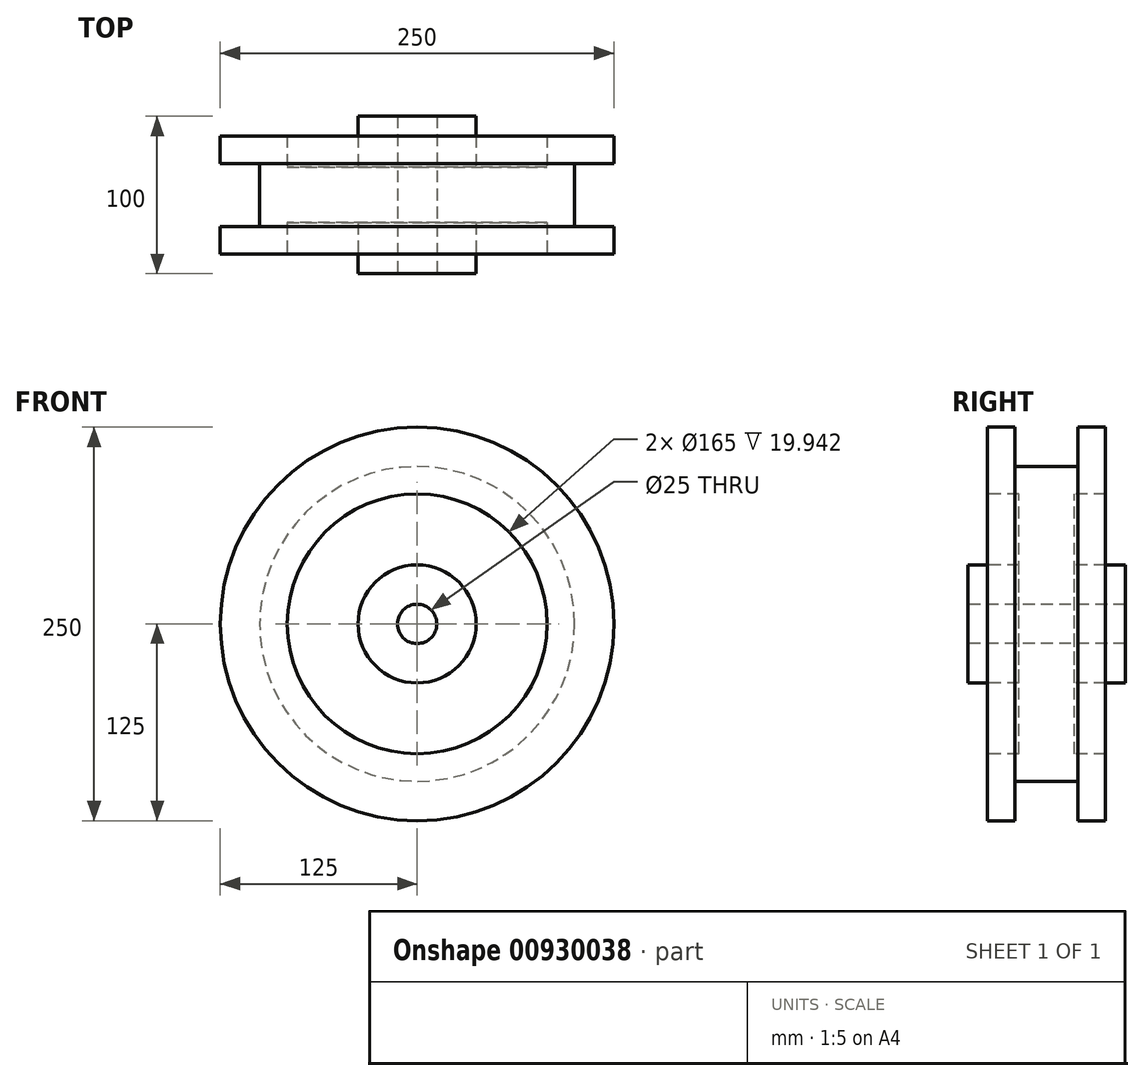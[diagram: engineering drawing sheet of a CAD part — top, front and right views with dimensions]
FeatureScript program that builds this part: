
annotation { "Feature Type Name" : "Feature", "Feature Type Description" : "" }
export const myFeature = defineFeature(function(context is Context, id is Id, definition is map)
    precondition{}
    {
        {
            var Q0;
            Q0=qCreatedBy(makeId("Right.planeOp"),FACE);
            var sketch = newSketch(context, id + "F0", { "sketchPlane" : qUnion([Q0])});
            skLineSegment(sketch, "E0", {"start": v(-83.35, 0) * mm, "end": v(75.08, 0) * mm, "construction": true});
            skLineSegment(sketch, "E1", {"start": v(0, 0) * mm, "end": v(0, 73.26) * mm, "construction": true});
            skLineSegment(sketch, "E2", {"start": v(-37.5, 125) * mm, "end": v(-20, 125) * mm});
            skLineSegment(sketch, "E3", {"start": v(-20, 125) * mm, "end": v(-20, 100) * mm});
            skLineSegment(sketch, "E4", {"start": v(-37.5, 125) * mm, "end": v(-37.5, 82.5) * mm});
            skLineSegment(sketch, "E5", {"start": v(-37.5, 82.5) * mm, "end": v(-17.56, 82.5) * mm});
            skLineSegment(sketch, "E6", {"start": v(-17.56, 82.5) * mm, "end": v(-17.56, 37.5) * mm});
            skLineSegment(sketch, "E7", {"start": v(-17.56, 37.5) * mm, "end": v(-50, 37.5) * mm});
            skLineSegment(sketch, "E8", {"start": v(-50, 37.5) * mm, "end": v(-50, 12.5) * mm});
            skLineSegment(sketch, "E9", {"start": v(-50, 12.5) * mm, "end": v(0, 12.5) * mm});
            skLineSegment(sketch, "E10.MirrorCS", {"start": v(37.5, 82.5) * mm, "end": v(17.56, 82.5) * mm});
            skLineSegment(sketch, "E11.MirrorCS", {"start": v(37.5, 125) * mm, "end": v(37.5, 82.5) * mm});
            skLineSegment(sketch, "E12.MirrorCS", {"start": v(50, 12.5) * mm, "end": v(0, 12.5) * mm});
            skLineSegment(sketch, "E13.MirrorCS", {"start": v(50, 37.5) * mm, "end": v(50, 12.5) * mm});
            skLineSegment(sketch, "E14.MirrorCS", {"start": v(20, 125) * mm, "end": v(20, 100) * mm});
            skLineSegment(sketch, "E15.MirrorCS", {"start": v(17.56, 37.5) * mm, "end": v(50, 37.5) * mm});
            skLineSegment(sketch, "E16.MirrorCS", {"start": v(37.5, 125) * mm, "end": v(20, 125) * mm});
            skLineSegment(sketch, "E17.MirrorCS", {"start": v(17.56, 82.5) * mm, "end": v(17.56, 37.5) * mm});
            skLineSegment(sketch, "E18", {"start": v(-20, 100) * mm, "end": v(0, 100) * mm});
            skLineSegment(sketch, "E19.MirrorCS", {"start": v(20, 100) * mm, "end": v(0, 100) * mm});
            skSolve(sketch);
        }
        {
            var Q0;
            Q0=makeQuery(id+"F0.imprint","IMPRINT",FACE,{"disambiguationData":[TD([[makeQuery(id+"F0.imprint","IMPRINT",EDGE,{"derivedFrom":sQuery(id+"F0.wireOp",EDGE,"E2")}),-1.0]])]});
            var Q1;
            Q1=sQuery(id+"F0.wireOp",EDGE,"E0");
            revolve(context, id + "F1", {"surfaceOperationType" : NewSurfaceOperationType.NEW, "entities" : qUnion([Q0]), "axis" : qUnion([Q1]), "revolveType" : RevolveType.FULL});
        }
    });
